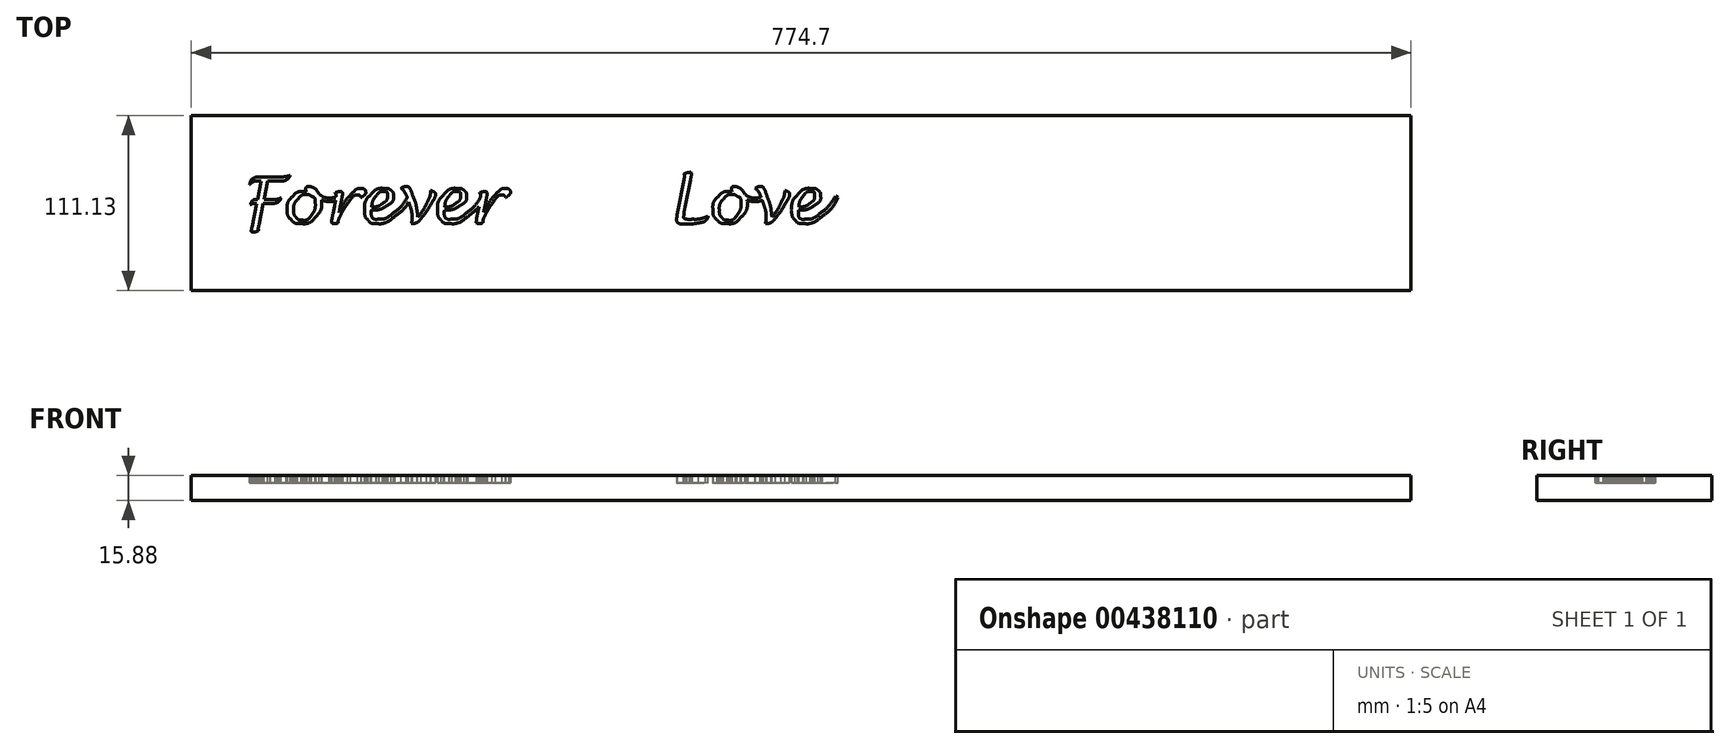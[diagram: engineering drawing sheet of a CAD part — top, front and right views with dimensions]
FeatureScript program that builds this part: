
annotation { "Feature Type Name" : "Feature", "Feature Type Description" : "" }
export const myFeature = defineFeature(function(context is Context, id is Id, definition is map)
    precondition{}
    {
        {
            var Q0;
            Q0=qCreatedBy(makeId("Top.planeOp"),FACE);
            var sketch = newSketch(context, id + "F0", { "sketchPlane" : qUnion([Q0])});
            skLineSegment(sketch, "E0.bottom", {"start": v(0, 0) * mm, "end": v(774.7, 0) * mm});
            skLineSegment(sketch, "E0.top", {"start": v(0, 111.13) * mm, "end": v(774.7, 111.13) * mm});
            skLineSegment(sketch, "E0.left", {"start": v(0, 0) * mm, "end": v(0, 111.13) * mm});
            skLineSegment(sketch, "E0.right", {"start": v(774.7, 0) * mm, "end": v(774.7, 111.13) * mm});
            skSolve(sketch);
        }
        {
            var Q0;
            Q0 = qSketchRegion(id + "F0", true);
            extrude(context, id + "F1", {"entities" : qUnion([Q0]), "depth" : 15.88 * mm});
        }
        {
            var Q0;
            Q0=makeQuery(id+"F1.opExtrude","CAP_FACE",FACE,{"disambiguationData":[OSD([sQuery(id+"F0.wireOp",EDGE,"E0.bottom"),sQuery(id+"F0.wireOp",EDGE,"E0.top"),sQuery(id+"F0.wireOp",EDGE,"E0.left"),sQuery(id+"F0.wireOp",EDGE,"E0.right")])],"isStart":false});
            var sketch = newSketch(context, id + "F2", { "sketchPlane" : qUnion([Q0])});
            skLineSegment(sketch, "E1.0", {"start": v(0, 0) * mm, "end": v(0, 111.13) * mm, "construction": true});
            skLineSegment(sketch, "E2.0", {"start": v(241.3, 0) * mm, "end": v(241.3, 111.13) * mm, "construction": true});
            skLineSegment(sketch, "E3.0", {"start": v(482.6, 0) * mm, "end": v(482.6, 111.13) * mm, "construction": true});
            skLineSegment(sketch, "E4.0", {"start": v(723.9, 0) * mm, "end": v(723.9, 111.13) * mm, "construction": true});
            skFitSpline(sketch, "E5", {"points": [v(42.88, 41.71) * mm, v(42.63, 40.47) * mm, v(42.51, 39.66) * mm, v(42.51, 39.3) * mm]});
            skFitSpline(sketch, "E6", {"points": [v(42.51, 39.3) * mm, v(42.51, 38.92) * mm, v(42.6, 38.53) * mm, v(42.77, 38.1) * mm]});
            skFitSpline(sketch, "E7", {"points": [v(42.77, 38.1) * mm, v(41.44, 37.44) * mm, v(40.23, 37.1) * mm, v(39.12, 37.1) * mm]});
            skFitSpline(sketch, "E8", {"points": [v(39.12, 37.1) * mm, v(38.44, 37.1) * mm, v(38.1, 37.38) * mm, v(38.1, 37.93) * mm]});
            skFitSpline(sketch, "E9", {"points": [v(38.1, 37.93) * mm, v(38.1, 38.22) * mm, v(38.23, 39.03) * mm, v(38.5, 40.37) * mm]});
            skLineSegment(sketch, "E10", {"start": v(45.6, 55.32) * mm, "end": v(42.88, 41.71) * mm});
            skFitSpline(sketch, "E11", {"points": [v(41.17, 55.32) * mm, v(39.99, 55.32) * mm, v(38.72, 55.04) * mm, v(37.35, 54.47) * mm]});
            skFitSpline(sketch, "E12", {"points": [v(37.35, 54.47) * mm, v(38, 55.86) * mm, v(38.56, 56.75) * mm, v(39.04, 57.15) * mm]});
            skFitSpline(sketch, "E13", {"points": [v(39.04, 57.15) * mm, v(39.54, 57.56) * mm, v(40.33, 57.76) * mm, v(41.4, 57.76) * mm]});
            skLineSegment(sketch, "E14", {"start": v(38.5, 40.37) * mm, "end": v(41.47, 55.32) * mm});
            skLineSegment(sketch, "E15", {"start": v(41.47, 55.32) * mm, "end": v(41.17, 55.32) * mm});
            skFitSpline(sketch, "E16", {"points": [v(43.87, 69.53) * mm, v(41, 69.53) * mm, v(38.73, 68.75) * mm, v(37.04, 67.19) * mm]});
            skFitSpline(sketch, "E17", {"points": [v(37.04, 67.19) * mm, v(37.55, 69.26) * mm, v(38.43, 70.65) * mm, v(39.7, 71.34) * mm]});
            skFitSpline(sketch, "E18", {"points": [v(39.7, 71.34) * mm, v(40.59, 71.83) * mm, v(43.36, 72.07) * mm, v(48, 72.07) * mm]});
            skLineSegment(sketch, "E19", {"start": v(41.4, 57.76) * mm, "end": v(41.94, 57.76) * mm});
            skLineSegment(sketch, "E20", {"start": v(41.94, 57.76) * mm, "end": v(44.3, 69.53) * mm});
            skLineSegment(sketch, "E21", {"start": v(44.3, 69.53) * mm, "end": v(43.87, 69.53) * mm});
            skFitSpline(sketch, "E22", {"points": [v(53.18, 72.07) * mm, v(57.04, 72.07) * mm, v(60.25, 72.41) * mm, v(62.8, 73.1) * mm]});
            skFitSpline(sketch, "E23", {"points": [v(62.8, 73.1) * mm, v(62, 71.67) * mm, v(61.14, 70.7) * mm, v(60.25, 70.22) * mm]});
            skFitSpline(sketch, "E24", {"points": [v(60.25, 70.22) * mm, v(59.37, 69.75) * mm, v(58.01, 69.51) * mm, v(56.17, 69.51) * mm]});
            skLineSegment(sketch, "E25", {"start": v(48, 72.07) * mm, "end": v(53.18, 72.07) * mm});
            skFitSpline(sketch, "E26", {"points": [v(50.33, 57.76) * mm, v(52.96, 57.76) * mm, v(55.14, 58.1) * mm, v(56.86, 58.76) * mm]});
            skFitSpline(sketch, "E27", {"points": [v(56.86, 58.76) * mm, v(56.23, 57.28) * mm, v(55.5, 56.34) * mm, v(54.68, 55.93) * mm]});
            skFitSpline(sketch, "E28", {"points": [v(54.68, 55.93) * mm, v(53.86, 55.52) * mm, v(52.26, 55.32) * mm, v(49.85, 55.32) * mm]});
            skLineSegment(sketch, "E29", {"start": v(56.17, 69.51) * mm, "end": v(54.44, 69.53) * mm});
            skLineSegment(sketch, "E30", {"start": v(54.44, 69.53) * mm, "end": v(48.42, 69.53) * mm});
            skLineSegment(sketch, "E31", {"start": v(48.42, 69.53) * mm, "end": v(46.07, 57.76) * mm});
            skLineSegment(sketch, "E32", {"start": v(46.07, 57.76) * mm, "end": v(50.33, 57.76) * mm});
            skFitSpline(sketch, "E33", {"points": [v(82.66, 57.44) * mm, v(82.7, 57.13) * mm, v(82.71, 56.85) * mm, v(82.71, 56.6) * mm]});
            skFitSpline(sketch, "E34", {"points": [v(82.71, 56.6) * mm, v(82.71, 52.8) * mm, v(81.43, 49.5) * mm, v(78.86, 46.67) * mm]});
            skFitSpline(sketch, "E35", {"points": [v(78.86, 46.67) * mm, v(76.28, 43.85) * mm, v(73.27, 42.44) * mm, v(69.82, 42.44) * mm]});
            skFitSpline(sketch, "E36", {"points": [v(69.82, 42.44) * mm, v(67.18, 42.44) * mm, v(65.03, 43.28) * mm, v(63.36, 44.96) * mm]});
            skFitSpline(sketch, "E37", {"points": [v(63.36, 44.96) * mm, v(61.7, 46.65) * mm, v(60.88, 48.85) * mm, v(60.88, 51.54) * mm]});
            skFitSpline(sketch, "E38", {"points": [v(60.88, 51.54) * mm, v(60.88, 54.6) * mm, v(61.95, 57.25) * mm, v(64.09, 59.5) * mm]});
            skFitSpline(sketch, "E39", {"points": [v(64.09, 59.5) * mm, v(66.24, 61.74) * mm, v(68.77, 62.86) * mm, v(71.69, 62.86) * mm]});
            skFitSpline(sketch, "E40", {"points": [v(71.69, 62.86) * mm, v(72.13, 62.86) * mm, v(72.6, 62.8) * mm, v(73.1, 62.68) * mm]});
            skFitSpline(sketch, "E41", {"points": [v(73.1, 62.68) * mm, v(72.78, 63.27) * mm, v(72.61, 63.77) * mm, v(72.61, 64.18) * mm]});
            skFitSpline(sketch, "E42", {"points": [v(72.61, 64.18) * mm, v(72.61, 64.8) * mm, v(72.83, 65.41) * mm, v(73.26, 65.99) * mm]});
            skFitSpline(sketch, "E43", {"points": [v(73.26, 65.99) * mm, v(76.47, 65.73) * mm, v(79.13, 64.09) * mm, v(81.26, 61.07) * mm]});
            skFitSpline(sketch, "E44", {"points": [v(81.26, 61.07) * mm, v(83.44, 59.58) * mm, v(85.7, 58.84) * mm, v(88.07, 58.84) * mm]});
            skFitSpline(sketch, "E45", {"points": [v(88.07, 58.84) * mm, v(89.6, 58.84) * mm, v(91.27, 59.36) * mm, v(93.05, 60.4) * mm]});
            skLineSegment(sketch, "E46", {"start": v(49.85, 55.32) * mm, "end": v(45.6, 55.32) * mm});
            skFitSpline(sketch, "E47", {"points": [v(94.04, 58.72) * mm, v(91.95, 57.27) * mm, v(89.8, 56.54) * mm, v(87.62, 56.54) * mm]});
            skFitSpline(sketch, "E48", {"points": [v(87.62, 56.54) * mm, v(86.16, 56.54) * mm, v(84.5, 56.84) * mm, v(82.66, 57.44) * mm]});
            skLineSegment(sketch, "E49", {"start": v(93.05, 60.4) * mm, "end": v(94.04, 58.72) * mm});
            skFitSpline(sketch, "E50", {"points": [v(78.19, 59.12) * mm, v(77.1, 59.45) * mm, v(76.1, 59.97) * mm, v(75.17, 60.7) * mm]});
            skFitSpline(sketch, "E51", {"points": [v(75.17, 60.7) * mm, v(74.5, 60.84) * mm, v(73.95, 60.9) * mm, v(73.5, 60.9) * mm]});
            skFitSpline(sketch, "E52", {"points": [v(73.5, 60.9) * mm, v(71.27, 60.9) * mm, v(69.29, 59.9) * mm, v(67.55, 57.9) * mm]});
            skFitSpline(sketch, "E53", {"points": [v(67.55, 57.9) * mm, v(65.83, 55.89) * mm, v(64.97, 53.6) * mm, v(64.97, 51.03) * mm]});
            skFitSpline(sketch, "E54", {"points": [v(64.97, 51.03) * mm, v(64.97, 49.16) * mm, v(65.5, 47.63) * mm, v(66.53, 46.42) * mm]});
            skFitSpline(sketch, "E55", {"points": [v(66.53, 46.42) * mm, v(67.58, 45.22) * mm, v(68.93, 44.63) * mm, v(70.57, 44.63) * mm]});
            skFitSpline(sketch, "E56", {"points": [v(70.57, 44.63) * mm, v(72.78, 44.63) * mm, v(74.7, 45.74) * mm, v(76.3, 47.97) * mm]});
            skFitSpline(sketch, "E57", {"points": [v(76.3, 47.97) * mm, v(77.9, 50.22) * mm, v(78.7, 52.89) * mm, v(78.7, 55.99) * mm]});
            skFitSpline(sketch, "E58", {"points": [v(78.7, 55.99) * mm, v(78.7, 57.06) * mm, v(78.53, 58.1) * mm, v(78.19, 59.12) * mm]});
            skFitSpline(sketch, "E59", {"points": [v(93.35, 43.07) * mm, v(92.45, 42.65) * mm, v(91.74, 42.44) * mm, v(91.2, 42.44) * mm]});
            skFitSpline(sketch, "E60", {"points": [v(91.2, 42.44) * mm, v(89.86, 42.44) * mm, v(89.2, 43.03) * mm, v(89.2, 44.21) * mm]});
            skFitSpline(sketch, "E61", {"points": [v(89.2, 44.21) * mm, v(89.2, 44.82) * mm, v(89.43, 46.32) * mm, v(89.9, 48.72) * mm]});
            skFitSpline(sketch, "E62", {"points": [v(90.89, 53.62) * mm, v(91.49, 56.54) * mm, v(91.8, 58.7) * mm, v(91.8, 60.1) * mm]});
            skFitSpline(sketch, "E63", {"points": [v(91.8, 60.1) * mm, v(91.8, 60.86) * mm, v(91.57, 61.5) * mm, v(91.14, 62.01) * mm]});
            skFitSpline(sketch, "E64", {"points": [v(91.14, 62.01) * mm, v(92.52, 62.48) * mm, v(93.64, 62.72) * mm, v(94.5, 62.72) * mm]});
            skFitSpline(sketch, "E65", {"points": [v(94.5, 62.72) * mm, v(95.43, 62.72) * mm, v(95.89, 62.14) * mm, v(95.89, 60.97) * mm]});
            skFitSpline(sketch, "E66", {"points": [v(95.89, 60.97) * mm, v(95.89, 60.25) * mm, v(95.56, 58.35) * mm, v(94.9, 55.28) * mm]});
            skLineSegment(sketch, "E67", {"start": v(89.9, 48.72) * mm, "end": v(90.89, 53.62) * mm});
            skFitSpline(sketch, "E68", {"points": [v(93.78, 49.55) * mm, v(96.26, 54.37) * mm, v(98.75, 58.1) * mm, v(101.26, 60.77) * mm]});
            skFitSpline(sketch, "E69", {"points": [v(101.26, 60.77) * mm, v(103.78, 63.45) * mm, v(106.07, 64.79) * mm, v(108.11, 64.79) * mm]});
            skFitSpline(sketch, "E70", {"points": [v(108.11, 64.79) * mm, v(108.83, 64.79) * mm, v(109.46, 64.58) * mm, v(109.98, 64.16) * mm]});
            skFitSpline(sketch, "E71", {"points": [v(109.98, 64.16) * mm, v(110.5, 63.75) * mm, v(110.77, 63.25) * mm, v(110.77, 62.66) * mm]});
            skFitSpline(sketch, "E72", {"points": [v(110.77, 62.66) * mm, v(110.77, 61.74) * mm, v(109.77, 60.52) * mm, v(107.78, 59) * mm]});
            skFitSpline(sketch, "E73", {"points": [v(107.78, 59) * mm, v(107.28, 60.04) * mm, v(106.57, 60.55) * mm, v(105.65, 60.55) * mm]});
            skFitSpline(sketch, "E74", {"points": [v(105.65, 60.55) * mm, v(103.98, 60.55) * mm, v(101.86, 58.78) * mm, v(99.27, 55.24) * mm]});
            skFitSpline(sketch, "E75", {"points": [v(99.27, 55.24) * mm, v(97.67, 53.03) * mm, v(96.28, 50.76) * mm, v(95.1, 48.4) * mm]});
            skFitSpline(sketch, "E76", {"points": [v(95.1, 48.4) * mm, v(93.92, 46.07) * mm, v(93.33, 44.4) * mm, v(93.33, 43.4) * mm]});
            skLineSegment(sketch, "E77", {"start": v(94.9, 55.28) * mm, "end": v(93.78, 49.55) * mm});
            skFitSpline(sketch, "E78", {"points": [v(114.35, 51.12) * mm, v(114.35, 47.28) * mm, v(115.98, 45.35) * mm, v(119.24, 45.35) * mm]});
            skFitSpline(sketch, "E79", {"points": [v(119.24, 45.35) * mm, v(122.06, 45.35) * mm, v(125.17, 46.7) * mm, v(128.57, 49.4) * mm]});
            skFitSpline(sketch, "E80", {"points": [v(128.57, 49.4) * mm, v(131.97, 52.08) * mm, v(135.03, 55.63) * mm, v(137.76, 60.02) * mm]});
            skLineSegment(sketch, "E81", {"start": v(93.33, 43.4) * mm, "end": v(93.35, 43.07) * mm});
            skFitSpline(sketch, "E82", {"points": [v(139.44, 59.1) * mm, v(136.87, 54.3) * mm, v(133.52, 50.32) * mm, v(129.4, 47.17) * mm]});
            skFitSpline(sketch, "E83", {"points": [v(129.4, 47.17) * mm, v(125.29, 44.02) * mm, v(121.39, 42.44) * mm, v(117.7, 42.44) * mm]});
            skFitSpline(sketch, "E84", {"points": [v(117.7, 42.44) * mm, v(115.34, 42.44) * mm, v(113.47, 43.2) * mm, v(112.1, 44.72) * mm]});
            skFitSpline(sketch, "E85", {"points": [v(112.1, 44.72) * mm, v(110.72, 46.25) * mm, v(110.04, 48.33) * mm, v(110.04, 50.97) * mm]});
            skFitSpline(sketch, "E86", {"points": [v(110.04, 50.97) * mm, v(110.04, 54.77) * mm, v(111.28, 58.03) * mm, v(113.76, 60.73) * mm]});
            skFitSpline(sketch, "E87", {"points": [v(113.76, 60.73) * mm, v(116.26, 63.44) * mm, v(119.26, 64.79) * mm, v(122.76, 64.79) * mm]});
            skFitSpline(sketch, "E88", {"points": [v(122.76, 64.79) * mm, v(124.45, 64.79) * mm, v(125.8, 64.36) * mm, v(126.82, 63.5) * mm]});
            skFitSpline(sketch, "E89", {"points": [v(126.82, 63.5) * mm, v(127.84, 62.65) * mm, v(128.35, 61.51) * mm, v(128.35, 60.08) * mm]});
            skFitSpline(sketch, "E90", {"points": [v(128.35, 60.08) * mm, v(128.35, 57.73) * mm, v(126.94, 55.65) * mm, v(124.1, 53.84) * mm]});
            skFitSpline(sketch, "E91", {"points": [v(124.1, 53.84) * mm, v(121.28, 52.03) * mm, v(118.03, 51.12) * mm, v(114.35, 51.12) * mm]});
            skLineSegment(sketch, "E92", {"start": v(137.76, 60.02) * mm, "end": v(139.44, 59.1) * mm});
            skFitSpline(sketch, "E93", {"points": [v(114.51, 53.01) * mm, v(117.25, 53.16) * mm, v(119.6, 53.95) * mm, v(121.56, 55.38) * mm]});
            skFitSpline(sketch, "E94", {"points": [v(121.56, 55.38) * mm, v(123.53, 56.8) * mm, v(124.51, 58.46) * mm, v(124.51, 60.34) * mm]});
            skFitSpline(sketch, "E95", {"points": [v(124.51, 60.34) * mm, v(124.51, 62.02) * mm, v(123.77, 62.86) * mm, v(122.27, 62.86) * mm]});
            skFitSpline(sketch, "E96", {"points": [v(122.27, 62.86) * mm, v(120.48, 62.86) * mm, v(118.84, 61.9) * mm, v(117.33, 59.98) * mm]});
            skFitSpline(sketch, "E97", {"points": [v(117.33, 59.98) * mm, v(115.82, 58.07) * mm, v(114.88, 55.74) * mm, v(114.51, 53.01) * mm]});
            skFitSpline(sketch, "E98", {"points": [v(139.65, 42.4) * mm, v(139.94, 43.56) * mm, v(140.09, 44.55) * mm, v(140.09, 45.4) * mm]});
            skFitSpline(sketch, "E99", {"points": [v(140.09, 45.4) * mm, v(140.09, 48.64) * mm, v(139.4, 52.22) * mm, v(138.02, 56.14) * mm]});
            skFitSpline(sketch, "E100", {"points": [v(138.02, 56.14) * mm, v(136.64, 60.07) * mm, v(135.03, 63.03) * mm, v(133.18, 65.02) * mm]});
            skFitSpline(sketch, "E101", {"points": [v(133.18, 65.02) * mm, v(134.32, 65.6) * mm, v(135.34, 65.9) * mm, v(136.25, 65.9) * mm]});
            skFitSpline(sketch, "E102", {"points": [v(136.25, 65.9) * mm, v(137.7, 65.9) * mm, v(139.15, 64) * mm, v(140.62, 60.2) * mm]});
            skFitSpline(sketch, "E103", {"points": [v(140.62, 60.2) * mm, v(142.1, 56.42) * mm, v(143.17, 51.85) * mm, v(143.8, 46.48) * mm]});
            skFitSpline(sketch, "E104", {"points": [v(143.8, 46.48) * mm, v(146.1, 49.4) * mm, v(148, 52.4) * mm, v(149.5, 55.5) * mm]});
            skFitSpline(sketch, "E105", {"points": [v(149.5, 55.5) * mm, v(151, 58.6) * mm, v(151.84, 61.26) * mm, v(152.04, 63.5) * mm]});
            skFitSpline(sketch, "E106", {"points": [v(152.04, 63.5) * mm, v(154, 62.72) * mm, v(155, 61.83) * mm, v(155, 60.83) * mm]});
            skFitSpline(sketch, "E107", {"points": [v(155, 60.83) * mm, v(155, 59.94) * mm, v(154.05, 57.92) * mm, v(152.16, 54.77) * mm]});
            skFitSpline(sketch, "E108", {"points": [v(152.16, 54.77) * mm, v(150.28, 51.62) * mm, v(148.24, 48.64) * mm, v(146.03, 45.83) * mm]});
            skFitSpline(sketch, "E109", {"points": [v(146.03, 45.83) * mm, v(144.96, 44.46) * mm, v(144.05, 43.58) * mm, v(143.32, 43.19) * mm]});
            skFitSpline(sketch, "E110", {"points": [v(143.32, 43.19) * mm, v(142.58, 42.8) * mm, v(141.36, 42.53) * mm, v(139.65, 42.4) * mm]});
            skFitSpline(sketch, "E111", {"points": [v(160.74, 51.12) * mm, v(160.74, 47.28) * mm, v(162.37, 45.35) * mm, v(165.62, 45.35) * mm]});
            skFitSpline(sketch, "E112", {"points": [v(165.62, 45.35) * mm, v(168.45, 45.35) * mm, v(171.56, 46.7) * mm, v(174.96, 49.4) * mm]});
            skFitSpline(sketch, "E113", {"points": [v(174.96, 49.4) * mm, v(178.36, 52.08) * mm, v(181.42, 55.63) * mm, v(184.15, 60.02) * mm]});
            skFitSpline(sketch, "E114", {"points": [v(185.82, 59.1) * mm, v(183.25, 54.3) * mm, v(179.9, 50.32) * mm, v(175.78, 47.17) * mm]});
            skFitSpline(sketch, "E115", {"points": [v(175.78, 47.17) * mm, v(171.67, 44.02) * mm, v(167.78, 42.44) * mm, v(164.09, 42.44) * mm]});
            skFitSpline(sketch, "E116", {"points": [v(164.09, 42.44) * mm, v(161.73, 42.44) * mm, v(159.85, 43.2) * mm, v(158.48, 44.72) * mm]});
            skFitSpline(sketch, "E117", {"points": [v(158.48, 44.72) * mm, v(157.11, 46.25) * mm, v(156.43, 48.33) * mm, v(156.43, 50.97) * mm]});
            skFitSpline(sketch, "E118", {"points": [v(156.43, 50.97) * mm, v(156.43, 54.77) * mm, v(157.67, 58.03) * mm, v(160.15, 60.73) * mm]});
            skFitSpline(sketch, "E119", {"points": [v(160.15, 60.73) * mm, v(162.64, 63.44) * mm, v(165.64, 64.79) * mm, v(169.15, 64.79) * mm]});
            skFitSpline(sketch, "E120", {"points": [v(169.15, 64.79) * mm, v(170.84, 64.79) * mm, v(172.2, 64.36) * mm, v(173.2, 63.5) * mm]});
            skFitSpline(sketch, "E121", {"points": [v(173.2, 63.5) * mm, v(174.23, 62.65) * mm, v(174.74, 61.51) * mm, v(174.74, 60.08) * mm]});
            skFitSpline(sketch, "E122", {"points": [v(174.74, 60.08) * mm, v(174.74, 57.73) * mm, v(173.32, 55.65) * mm, v(170.49, 53.84) * mm]});
            skFitSpline(sketch, "E123", {"points": [v(170.49, 53.84) * mm, v(167.66, 52.03) * mm, v(164.42, 51.12) * mm, v(160.74, 51.12) * mm]});
            skLineSegment(sketch, "E124", {"start": v(184.15, 60.02) * mm, "end": v(185.82, 59.1) * mm});
            skFitSpline(sketch, "E125", {"points": [v(160.9, 53.01) * mm, v(163.64, 53.16) * mm, v(166, 53.95) * mm, v(167.95, 55.38) * mm]});
            skFitSpline(sketch, "E126", {"points": [v(167.95, 55.38) * mm, v(169.92, 56.8) * mm, v(170.9, 58.46) * mm, v(170.9, 60.34) * mm]});
            skFitSpline(sketch, "E127", {"points": [v(170.9, 60.34) * mm, v(170.9, 62.02) * mm, v(170.15, 62.86) * mm, v(168.66, 62.86) * mm]});
            skFitSpline(sketch, "E128", {"points": [v(168.66, 62.86) * mm, v(166.87, 62.86) * mm, v(165.22, 61.9) * mm, v(163.71, 59.98) * mm]});
            skFitSpline(sketch, "E129", {"points": [v(163.71, 59.98) * mm, v(162.2, 58.07) * mm, v(161.27, 55.74) * mm, v(160.9, 53.01) * mm]});
            skFitSpline(sketch, "E130", {"points": [v(185.17, 43.07) * mm, v(184.28, 42.65) * mm, v(183.57, 42.44) * mm, v(183.03, 42.44) * mm]});
            skFitSpline(sketch, "E131", {"points": [v(183.03, 42.44) * mm, v(181.69, 42.44) * mm, v(181.02, 43.03) * mm, v(181.02, 44.21) * mm]});
            skFitSpline(sketch, "E132", {"points": [v(181.02, 44.21) * mm, v(181.02, 44.82) * mm, v(181.26, 46.32) * mm, v(181.73, 48.72) * mm]});
            skFitSpline(sketch, "E133", {"points": [v(182.71, 53.62) * mm, v(183.32, 56.54) * mm, v(183.62, 58.7) * mm, v(183.62, 60.1) * mm]});
            skFitSpline(sketch, "E134", {"points": [v(183.62, 60.1) * mm, v(183.62, 60.86) * mm, v(183.4, 61.5) * mm, v(182.97, 62.01) * mm]});
            skFitSpline(sketch, "E135", {"points": [v(182.97, 62.01) * mm, v(184.35, 62.48) * mm, v(185.47, 62.72) * mm, v(186.34, 62.72) * mm]});
            skFitSpline(sketch, "E136", {"points": [v(186.34, 62.72) * mm, v(187.26, 62.72) * mm, v(187.71, 62.14) * mm, v(187.71, 60.97) * mm]});
            skFitSpline(sketch, "E137", {"points": [v(187.71, 60.97) * mm, v(187.71, 60.25) * mm, v(187.39, 58.35) * mm, v(186.73, 55.28) * mm]});
            skLineSegment(sketch, "E138", {"start": v(181.73, 48.72) * mm, "end": v(182.71, 53.62) * mm});
            skFitSpline(sketch, "E139", {"points": [v(185.6, 49.55) * mm, v(188.09, 54.37) * mm, v(190.58, 58.1) * mm, v(193.09, 60.77) * mm]});
            skFitSpline(sketch, "E140", {"points": [v(193.09, 60.77) * mm, v(195.6, 63.45) * mm, v(197.9, 64.79) * mm, v(199.94, 64.79) * mm]});
            skFitSpline(sketch, "E141", {"points": [v(199.94, 64.79) * mm, v(200.66, 64.79) * mm, v(201.29, 64.58) * mm, v(201.81, 64.16) * mm]});
            skFitSpline(sketch, "E142", {"points": [v(201.81, 64.16) * mm, v(202.34, 63.75) * mm, v(202.6, 63.25) * mm, v(202.6, 62.66) * mm]});
            skFitSpline(sketch, "E143", {"points": [v(202.6, 62.66) * mm, v(202.6, 61.74) * mm, v(201.6, 60.52) * mm, v(199.6, 59) * mm]});
            skFitSpline(sketch, "E144", {"points": [v(199.6, 59) * mm, v(199.1, 60.04) * mm, v(198.4, 60.55) * mm, v(197.48, 60.55) * mm]});
            skFitSpline(sketch, "E145", {"points": [v(197.48, 60.55) * mm, v(195.81, 60.55) * mm, v(193.69, 58.78) * mm, v(191.1, 55.24) * mm]});
            skFitSpline(sketch, "E146", {"points": [v(191.1, 55.24) * mm, v(189.5, 53.03) * mm, v(188.1, 50.76) * mm, v(186.93, 48.4) * mm]});
            skFitSpline(sketch, "E147", {"points": [v(186.93, 48.4) * mm, v(185.75, 46.07) * mm, v(185.15, 44.4) * mm, v(185.15, 43.4) * mm]});
            skLineSegment(sketch, "E148", {"start": v(186.73, 55.28) * mm, "end": v(185.6, 49.55) * mm});
            skFitSpline(sketch, "E149", {"points": [v(328.26, 47.23) * mm, v(327.82, 45.94) * mm, v(327.31, 45) * mm, v(326.72, 44.4) * mm]});
            skFitSpline(sketch, "E150", {"points": [v(326.72, 44.4) * mm, v(326.13, 43.82) * mm, v(324.63, 43.3) * mm, v(322.23, 42.87) * mm]});
            skFitSpline(sketch, "E151", {"points": [v(322.23, 42.87) * mm, v(319.84, 42.43) * mm, v(317.31, 42.2) * mm, v(314.65, 42.2) * mm]});
            skFitSpline(sketch, "E152", {"points": [v(314.65, 42.2) * mm, v(310.46, 42.2) * mm, v(308.37, 43.64) * mm, v(308.37, 46.5) * mm]});
            skFitSpline(sketch, "E153", {"points": [v(308.37, 46.5) * mm, v(308.37, 47.3) * mm, v(308.6, 48.81) * mm, v(309.04, 51.04) * mm]});
            skLineSegment(sketch, "E154", {"start": v(185.15, 43.4) * mm, "end": v(185.17, 43.07) * mm});
            skFitSpline(sketch, "E155", {"points": [v(312.88, 70.38) * mm, v(313.1, 71.5) * mm, v(313.21, 72.3) * mm, v(313.21, 72.78) * mm]});
            skFitSpline(sketch, "E156", {"points": [v(313.21, 72.78) * mm, v(313.21, 73.23) * mm, v(313.06, 73.64) * mm, v(312.74, 74.02) * mm]});
            skFitSpline(sketch, "E157", {"points": [v(312.74, 74.02) * mm, v(314.49, 74.68) * mm, v(315.7, 75) * mm, v(316.38, 75) * mm]});
            skFitSpline(sketch, "E158", {"points": [v(316.38, 75) * mm, v(317.2, 75) * mm, v(317.6, 74.54) * mm, v(317.6, 73.6) * mm]});
            skFitSpline(sketch, "E159", {"points": [v(317.6, 73.6) * mm, v(317.6, 73.37) * mm, v(317.39, 72.22) * mm, v(316.95, 70.14) * mm]});
            skLineSegment(sketch, "E160", {"start": v(309.04, 51.04) * mm, "end": v(312.88, 70.38) * mm});
            skFitSpline(sketch, "E161", {"points": [v(313.53, 52.88) * mm, v(313.03, 50.4) * mm, v(312.78, 48.67) * mm, v(312.78, 47.7) * mm]});
            skFitSpline(sketch, "E162", {"points": [v(312.78, 47.7) * mm, v(312.78, 46.06) * mm, v(314.6, 45.24) * mm, v(318.23, 45.24) * mm]});
            skFitSpline(sketch, "E163", {"points": [v(318.23, 45.24) * mm, v(321.48, 45.24) * mm, v(324.82, 45.9) * mm, v(328.26, 47.23) * mm]});
            skLineSegment(sketch, "E164", {"start": v(316.95, 70.14) * mm, "end": v(313.53, 52.88) * mm});
            skFitSpline(sketch, "E165", {"points": [v(353, 57.44) * mm, v(353.04, 57.13) * mm, v(353.06, 56.85) * mm, v(353.06, 56.6) * mm]});
            skFitSpline(sketch, "E166", {"points": [v(353.06, 56.6) * mm, v(353.06, 52.8) * mm, v(351.78, 49.5) * mm, v(349.2, 46.67) * mm]});
            skFitSpline(sketch, "E167", {"points": [v(349.2, 46.67) * mm, v(346.63, 43.85) * mm, v(343.62, 42.44) * mm, v(340.17, 42.44) * mm]});
            skFitSpline(sketch, "E168", {"points": [v(340.17, 42.44) * mm, v(337.53, 42.44) * mm, v(335.38, 43.28) * mm, v(333.7, 44.96) * mm]});
            skFitSpline(sketch, "E169", {"points": [v(333.7, 44.96) * mm, v(332.06, 46.65) * mm, v(331.23, 48.85) * mm, v(331.23, 51.54) * mm]});
            skFitSpline(sketch, "E170", {"points": [v(331.23, 51.54) * mm, v(331.23, 54.6) * mm, v(332.3, 57.25) * mm, v(334.44, 59.5) * mm]});
            skFitSpline(sketch, "E171", {"points": [v(334.44, 59.5) * mm, v(336.6, 61.74) * mm, v(339.12, 62.86) * mm, v(342.04, 62.86) * mm]});
            skFitSpline(sketch, "E172", {"points": [v(342.04, 62.86) * mm, v(342.48, 62.86) * mm, v(342.96, 62.8) * mm, v(343.45, 62.68) * mm]});
            skFitSpline(sketch, "E173", {"points": [v(343.45, 62.68) * mm, v(343.13, 63.27) * mm, v(342.96, 63.77) * mm, v(342.96, 64.18) * mm]});
            skFitSpline(sketch, "E174", {"points": [v(342.96, 64.18) * mm, v(342.96, 64.8) * mm, v(343.18, 65.41) * mm, v(343.61, 65.99) * mm]});
            skFitSpline(sketch, "E175", {"points": [v(343.61, 65.99) * mm, v(346.81, 65.73) * mm, v(349.48, 64.09) * mm, v(351.6, 61.07) * mm]});
            skFitSpline(sketch, "E176", {"points": [v(351.6, 61.07) * mm, v(353.78, 59.58) * mm, v(356.06, 58.84) * mm, v(358.42, 58.84) * mm]});
            skFitSpline(sketch, "E177", {"points": [v(358.42, 58.84) * mm, v(359.95, 58.84) * mm, v(361.61, 59.36) * mm, v(363.4, 60.4) * mm]});
            skFitSpline(sketch, "E178", {"points": [v(364.38, 58.72) * mm, v(362.3, 57.27) * mm, v(360.16, 56.54) * mm, v(357.97, 56.54) * mm]});
            skFitSpline(sketch, "E179", {"points": [v(357.97, 56.54) * mm, v(356.5, 56.54) * mm, v(354.85, 56.84) * mm, v(353, 57.44) * mm]});
            skLineSegment(sketch, "E180", {"start": v(363.4, 60.4) * mm, "end": v(364.38, 58.72) * mm});
            skFitSpline(sketch, "E181", {"points": [v(348.53, 59.12) * mm, v(347.45, 59.45) * mm, v(346.44, 59.97) * mm, v(345.52, 60.7) * mm]});
            skFitSpline(sketch, "E182", {"points": [v(345.52, 60.7) * mm, v(344.85, 60.84) * mm, v(344.3, 60.9) * mm, v(343.85, 60.9) * mm]});
            skFitSpline(sketch, "E183", {"points": [v(343.85, 60.9) * mm, v(341.62, 60.9) * mm, v(339.64, 59.9) * mm, v(337.9, 57.9) * mm]});
            skFitSpline(sketch, "E184", {"points": [v(337.9, 57.9) * mm, v(336.18, 55.89) * mm, v(335.32, 53.6) * mm, v(335.32, 51.03) * mm]});
            skFitSpline(sketch, "E185", {"points": [v(335.32, 51.03) * mm, v(335.32, 49.16) * mm, v(335.84, 47.63) * mm, v(336.88, 46.42) * mm]});
            skFitSpline(sketch, "E186", {"points": [v(336.88, 46.42) * mm, v(337.93, 45.22) * mm, v(339.27, 44.63) * mm, v(340.92, 44.63) * mm]});
            skFitSpline(sketch, "E187", {"points": [v(340.92, 44.63) * mm, v(343.13, 44.63) * mm, v(345.04, 45.74) * mm, v(346.64, 47.97) * mm]});
            skFitSpline(sketch, "E188", {"points": [v(346.64, 47.97) * mm, v(348.25, 50.22) * mm, v(349.05, 52.89) * mm, v(349.05, 55.99) * mm]});
            skFitSpline(sketch, "E189", {"points": [v(349.05, 55.99) * mm, v(349.05, 57.06) * mm, v(348.88, 58.1) * mm, v(348.53, 59.12) * mm]});
            skFitSpline(sketch, "E190", {"points": [v(364.56, 42.4) * mm, v(364.85, 43.56) * mm, v(365, 44.55) * mm, v(365, 45.4) * mm]});
            skFitSpline(sketch, "E191", {"points": [v(365, 45.4) * mm, v(365, 48.64) * mm, v(364.3, 52.22) * mm, v(362.93, 56.14) * mm]});
            skFitSpline(sketch, "E192", {"points": [v(362.93, 56.14) * mm, v(361.55, 60.07) * mm, v(359.93, 63.03) * mm, v(358.08, 65.02) * mm]});
            skFitSpline(sketch, "E193", {"points": [v(358.08, 65.02) * mm, v(359.23, 65.6) * mm, v(360.25, 65.9) * mm, v(361.15, 65.9) * mm]});
            skFitSpline(sketch, "E194", {"points": [v(361.15, 65.9) * mm, v(362.6, 65.9) * mm, v(364.06, 64) * mm, v(365.53, 60.2) * mm]});
            skFitSpline(sketch, "E195", {"points": [v(365.53, 60.2) * mm, v(367, 56.42) * mm, v(368.07, 51.85) * mm, v(368.72, 46.48) * mm]});
            skFitSpline(sketch, "E196", {"points": [v(368.72, 46.48) * mm, v(371.01, 49.4) * mm, v(372.9, 52.4) * mm, v(374.4, 55.5) * mm]});
            skFitSpline(sketch, "E197", {"points": [v(374.4, 55.5) * mm, v(375.9, 58.6) * mm, v(376.75, 61.26) * mm, v(376.95, 63.5) * mm]});
            skFitSpline(sketch, "E198", {"points": [v(376.95, 63.5) * mm, v(378.91, 62.72) * mm, v(379.9, 61.83) * mm, v(379.9, 60.83) * mm]});
            skFitSpline(sketch, "E199", {"points": [v(379.9, 60.83) * mm, v(379.9, 59.94) * mm, v(378.95, 57.92) * mm, v(377.06, 54.77) * mm]});
            skFitSpline(sketch, "E200", {"points": [v(377.06, 54.77) * mm, v(375.19, 51.62) * mm, v(373.15, 48.64) * mm, v(370.94, 45.83) * mm]});
            skFitSpline(sketch, "E201", {"points": [v(370.94, 45.83) * mm, v(369.86, 44.46) * mm, v(368.96, 43.58) * mm, v(368.22, 43.19) * mm]});
            skFitSpline(sketch, "E202", {"points": [v(368.22, 43.19) * mm, v(367.49, 42.8) * mm, v(366.27, 42.53) * mm, v(364.56, 42.4) * mm]});
            skFitSpline(sketch, "E203", {"points": [v(385.65, 51.12) * mm, v(385.65, 47.28) * mm, v(387.28, 45.35) * mm, v(390.53, 45.35) * mm]});
            skFitSpline(sketch, "E204", {"points": [v(390.53, 45.35) * mm, v(393.35, 45.35) * mm, v(396.46, 46.7) * mm, v(399.86, 49.4) * mm]});
            skFitSpline(sketch, "E205", {"points": [v(399.86, 49.4) * mm, v(403.26, 52.08) * mm, v(406.33, 55.63) * mm, v(409.06, 60.02) * mm]});
            skFitSpline(sketch, "E206", {"points": [v(410.73, 59.1) * mm, v(408.16, 54.3) * mm, v(404.81, 50.32) * mm, v(400.7, 47.17) * mm]});
            skFitSpline(sketch, "E207", {"points": [v(400.7, 47.17) * mm, v(396.58, 44.02) * mm, v(392.68, 42.44) * mm, v(389, 42.44) * mm]});
            skFitSpline(sketch, "E208", {"points": [v(389, 42.44) * mm, v(386.63, 42.44) * mm, v(384.76, 43.2) * mm, v(383.38, 44.72) * mm]});
            skFitSpline(sketch, "E209", {"points": [v(383.38, 44.72) * mm, v(382.02, 46.25) * mm, v(381.34, 48.33) * mm, v(381.34, 50.97) * mm]});
            skFitSpline(sketch, "E210", {"points": [v(381.34, 50.97) * mm, v(381.34, 54.77) * mm, v(382.58, 58.03) * mm, v(385.06, 60.73) * mm]});
            skFitSpline(sketch, "E211", {"points": [v(385.06, 60.73) * mm, v(387.55, 63.44) * mm, v(390.55, 64.79) * mm, v(394.05, 64.79) * mm]});
            skFitSpline(sketch, "E212", {"points": [v(394.05, 64.79) * mm, v(395.75, 64.79) * mm, v(397.1, 64.36) * mm, v(398.11, 63.5) * mm]});
            skFitSpline(sketch, "E213", {"points": [v(398.11, 63.5) * mm, v(399.13, 62.65) * mm, v(399.65, 61.51) * mm, v(399.65, 60.08) * mm]});
            skFitSpline(sketch, "E214", {"points": [v(399.65, 60.08) * mm, v(399.65, 57.73) * mm, v(398.23, 55.65) * mm, v(395.4, 53.84) * mm]});
            skFitSpline(sketch, "E215", {"points": [v(395.4, 53.84) * mm, v(392.57, 52.03) * mm, v(389.32, 51.12) * mm, v(385.65, 51.12) * mm]});
            skLineSegment(sketch, "E216", {"start": v(409.06, 60.02) * mm, "end": v(410.73, 59.1) * mm});
            skFitSpline(sketch, "E217", {"points": [v(385.8, 53.01) * mm, v(388.55, 53.16) * mm, v(390.9, 53.95) * mm, v(392.85, 55.38) * mm]});
            skFitSpline(sketch, "E218", {"points": [v(392.85, 55.38) * mm, v(394.82, 56.8) * mm, v(395.8, 58.46) * mm, v(395.8, 60.34) * mm]});
            skFitSpline(sketch, "E219", {"points": [v(395.8, 60.34) * mm, v(395.8, 62.02) * mm, v(395.06, 62.86) * mm, v(393.56, 62.86) * mm]});
            skFitSpline(sketch, "E220", {"points": [v(393.56, 62.86) * mm, v(391.78, 62.86) * mm, v(390.13, 61.9) * mm, v(388.62, 59.98) * mm]});
            skFitSpline(sketch, "E221", {"points": [v(388.62, 59.98) * mm, v(387.11, 58.07) * mm, v(386.17, 55.74) * mm, v(385.8, 53.01) * mm]});
            skSolve(sketch);
        }
        {
            var Q0;
            Q0 = qSketchRegion(id + "F2", true);
            extrude(context, id + "F3", {"entities" : qUnion([Q0]), "operationType" : NewBodyOperationType.REMOVE, "oppositeDirection" : true, "depth" : 4.76 * mm});
        }
    });
